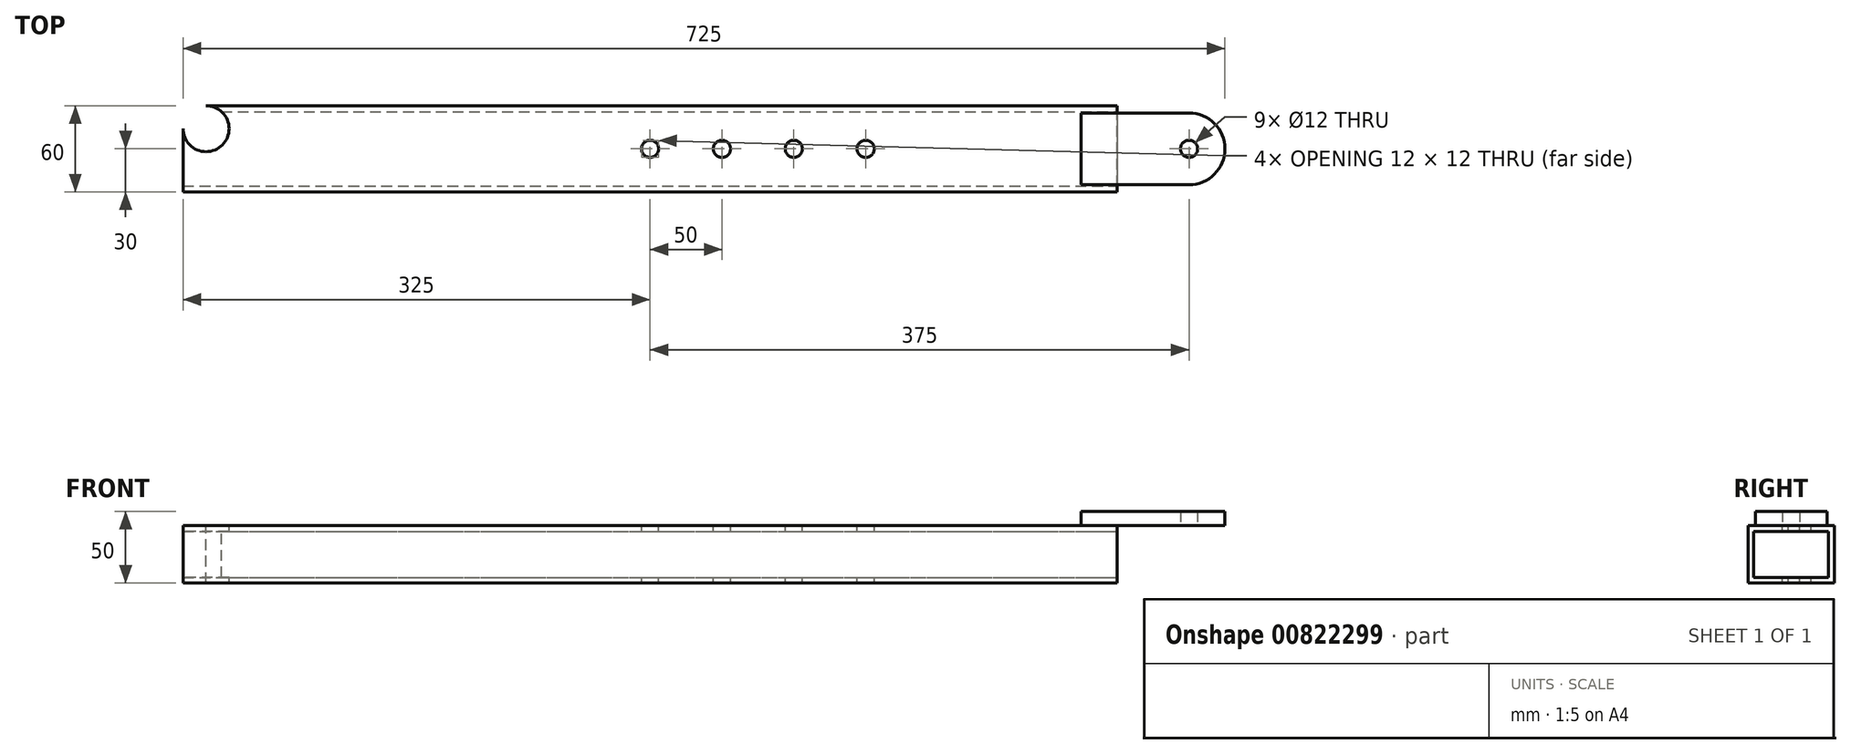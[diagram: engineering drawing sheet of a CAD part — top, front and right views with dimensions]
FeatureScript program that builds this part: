
annotation { "Feature Type Name" : "Feature", "Feature Type Description" : "" }
export const myFeature = defineFeature(function(context is Context, id is Id, definition is map)
    precondition{}
    {
        {
            var Q0;
            Q0=qCreatedBy(makeId("Top.planeOp"),FACE);
            var sketch = newSketch(context, id + "F0", { "sketchPlane" : qUnion([Q0])});
            skCircle(sketch, "E0", {"center": v(0, 0) * mm, "radius": 6 * mm});
            skCircle(sketch, "E1", {"center": v(0, 0) * mm, "radius": 25 * mm});
            skLineSegment(sketch, "E2", {"start": v(0, 25) * mm, "end": v(-50, 25) * mm});
            skLineSegment(sketch, "E3", {"start": v(0, -25) * mm, "end": v(-50, -25) * mm});
            skLineSegment(sketch, "E4", {"start": v(-50, 25) * mm, "end": v(-50, -25) * mm});
            skSolve(sketch);
        }
        {
            var Q0;
            Q0 = qSketchRegion(id + "F0", true);
            extrude(context, id + "F1", {"entities" : qUnion([Q0]), "depth" : 10 * mm, "offsetDistance" : 25 * mm});
        }
        {
            var Q0;
            Q0=makeQuery(id+"F1.opExtrude","SWEPT_FACE",FACE,{"disambiguationData":[OSD([sQuery(id+"F0.wireOp",EDGE,"E4")])]});
            var sketch = newSketch(context, id + "F2", { "sketchPlane" : qUnion([Q0])});
            skLineSegment(sketch, "E5", {"start": v(0, 0) * mm, "end": v(-30, 0) * mm});
            skLineSegment(sketch, "E6", {"start": v(-30, 0) * mm, "end": v(-30, -40) * mm});
            skLineSegment(sketch, "E7", {"start": v(-30, -40) * mm, "end": v(30, -40) * mm});
            skLineSegment(sketch, "E8", {"start": v(30, -40) * mm, "end": v(30, 0) * mm});
            skLineSegment(sketch, "E9", {"start": v(30, 0) * mm, "end": v(0, 0) * mm});
            skLineSegment(sketch, "E10.bottom", {"start": v(26, -36) * mm, "end": v(-26, -36) * mm});
            skLineSegment(sketch, "E10.top", {"start": v(26, -4) * mm, "end": v(-26, -4) * mm});
            skLineSegment(sketch, "E10.left", {"start": v(26, -36) * mm, "end": v(26, -4) * mm});
            skLineSegment(sketch, "E10.right", {"start": v(-26, -36) * mm, "end": v(-26, -4) * mm});
            skPoint(sketch, "E10.middle", {"position": v(0, -20) * mm});
            skPoint(sketch, "E10.middle.positionSnap0", {"position": v(30, -20) * mm});
            skPoint(sketch, "E10.centerSnap0", {"position": v(30, -20) * mm});
            skSolve(sketch);
        }
        {
            var Q0;
            Q0 = qSketchRegion(id + "F2", true);
            extrude(context, id + "F3", {"entities" : qUnion([Q0]), "depth" : 650 * mm, "offsetDistance" : 25 * mm});
        }
        {
            var Q0;
            Q0=makeQuery(id+"F1.opExtrude","SWEPT_FACE",FACE,{"disambiguationData":[OSD([sQuery(id+"F0.wireOp",EDGE,"E4")])]});
            extrude(context, id + "F4", {"entities" : qUnion([Q0]), "operationType" : NewBodyOperationType.ADD, "depth" : 25 * mm, "offsetDistance" : 25 * mm});
        }
        {
            var Q0;
            Q0=makeQuery(id+"F3.opExtrude","SWEPT_FACE",FACE,{"disambiguationData":[OSD([sQuery(id+"F2.wireOp",EDGE,"E5"),sQuery(id+"F2.wireOp",EDGE,"E9")])]});
            var sketch = newSketch(context, id + "F5", { "sketchPlane" : qUnion([Q0])});
            skLineSegment(sketch, "E11", {"start": v(-375, 30) * mm, "end": v(-375, 0) * mm});
            skLineSegment(sketch, "E12", {"start": v(-375, 0) * mm, "end": v(-325, 0) * mm});
            skLineSegment(sketch, "E13", {"start": v(-325, 0) * mm, "end": v(-275, 0) * mm});
            skLineSegment(sketch, "E14", {"start": v(-275, 0) * mm, "end": v(-225, 0) * mm});
            skCircle(sketch, "E15", {"center": v(-375, 0) * mm, "radius": 6 * mm});
            skCircle(sketch, "E16", {"center": v(-325, 0) * mm, "radius": 6 * mm});
            skCircle(sketch, "E17", {"center": v(-275, 0) * mm, "radius": 6 * mm});
            skCircle(sketch, "E18", {"center": v(-225, 0) * mm, "radius": 6 * mm});
            skSolve(sketch);
        }
        {
            var Q0;
            Q0 = qSketchRegion(id + "F5", true);
            extrude(context, id + "F6", {"entities" : qUnion([Q0]), "operationType" : NewBodyOperationType.REMOVE, "oppositeDirection" : true, "depth" : 40 * mm, "offsetDistance" : 25 * mm});
        }
        {
            var Q0;
            Q0=makeQuery(id+"F3.opExtrude","SWEPT_FACE",FACE,{"disambiguationData":[OSD([sQuery(id+"F2.wireOp",EDGE,"E5"),sQuery(id+"F2.wireOp",EDGE,"E9")])]});
            var sketch = newSketch(context, id + "F7", { "sketchPlane" : qUnion([Q0])});
            skLineSegment(sketch, "E19", {"start": v(-700, 30) * mm, "end": v(-684, 30) * mm});
            skLineSegment(sketch, "E20", {"start": v(-684, 30) * mm, "end": v(-684, 14) * mm});
            skCircle(sketch, "E21", {"center": v(-684, 14) * mm, "radius": 16 * mm});
            skLineSegment(sketch, "E22", {"start": v(-700, 30) * mm, "end": v(-700, 14) * mm});
            skSolve(sketch);
        }
        {
            var Q0;
            Q0 = qSketchRegion(id + "F7", true);
            extrude(context, id + "F8", {"entities" : qUnion([Q0]), "operationType" : NewBodyOperationType.REMOVE, "oppositeDirection" : true, "depth" : 40 * mm, "offsetDistance" : 25 * mm});
        }
    });
